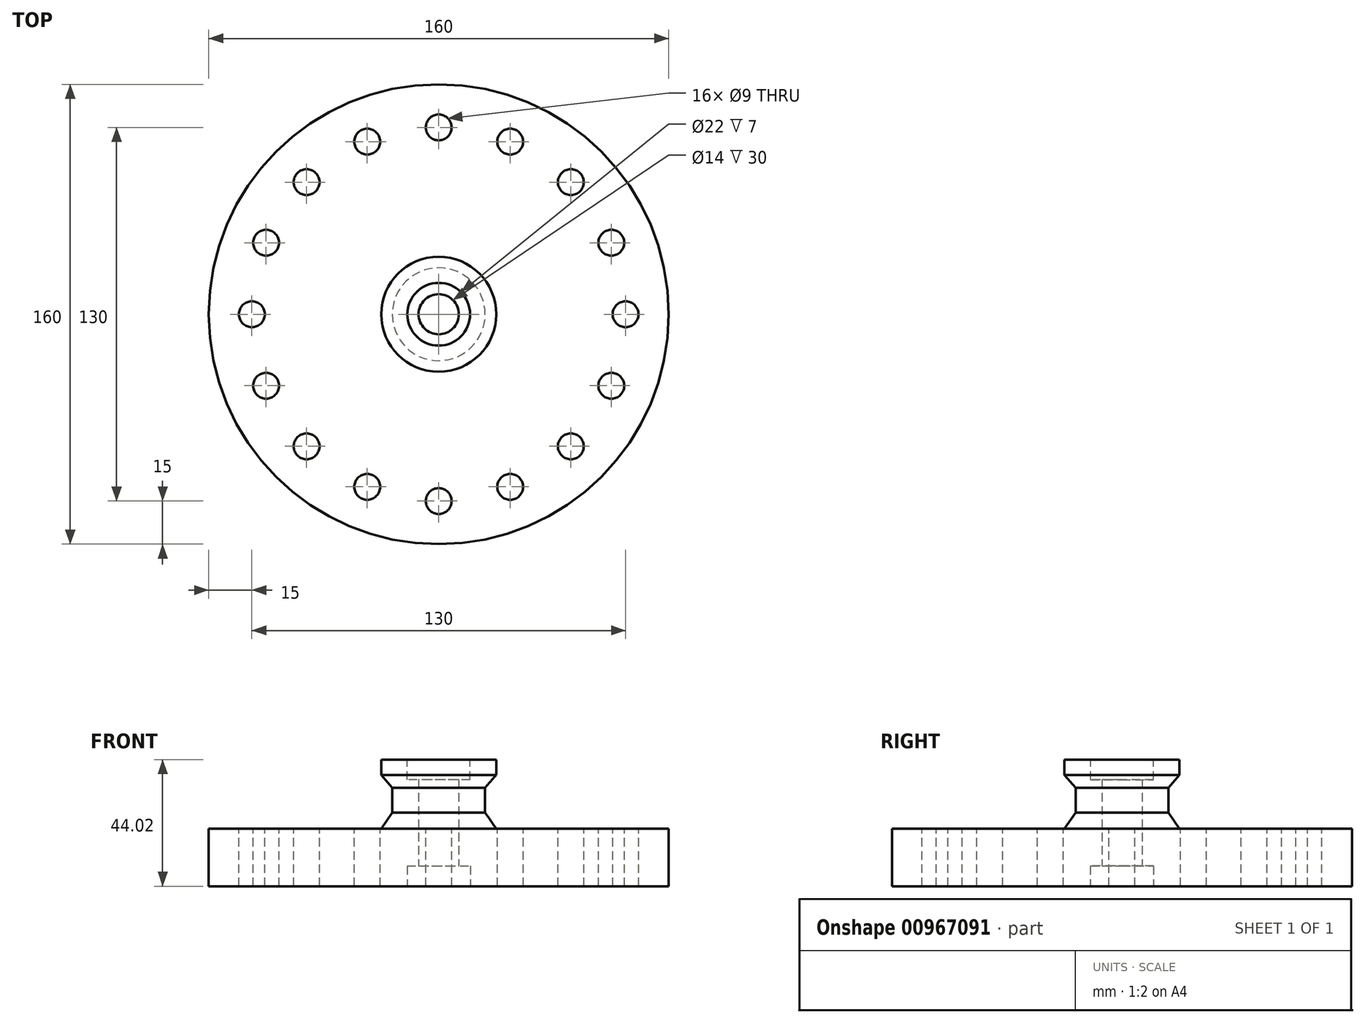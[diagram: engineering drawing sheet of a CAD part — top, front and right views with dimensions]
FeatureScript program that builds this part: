
annotation { "Feature Type Name" : "Feature", "Feature Type Description" : "" }
export const myFeature = defineFeature(function(context is Context, id is Id, definition is map)
    precondition{}
    {
        {
            var Q0;
            Q0=qCreatedBy(makeId("Front.planeOp"),FACE);
            var sketch = newSketch(context, id + "F0", { "sketchPlane" : qUnion([Q0])});
            skLineSegment(sketch, "E0.bottom", {"start": v(-80, 20) * mm, "end": v(-20, 20) * mm});
            skLineSegment(sketch, "E0.top", {"start": v(-80, 0) * mm, "end": v(0, 0) * mm});
            skLineSegment(sketch, "E0.left", {"start": v(-80, 20) * mm, "end": v(-80, 0) * mm});
            skLineSegment(sketch, "E0.right", {"start": v(0, 20) * mm, "end": v(0, 0) * mm});
            skLineSegment(sketch, "E1.left", {"start": v(-20, 38.7) * mm, "end": v(-20, 44.02) * mm});
            skLineSegment(sketch, "E1.right", {"start": v(0, 20) * mm, "end": v(0, 37) * mm});
            skLineSegment(sketch, "E2", {"start": v(0, 100.53) * mm, "end": v(0, 55) * mm, "construction": true});
            skLineSegment(sketch, "E3", {"start": v(-20, 38.7) * mm, "end": v(-16.15, 34.3) * mm});
            skLineSegment(sketch, "E4", {"start": v(-16.15, 34.3) * mm, "end": v(-16.15, 25.61) * mm});
            skLineSegment(sketch, "E5", {"start": v(-16.15, 25.61) * mm, "end": v(-20, 20) * mm});
            skLineSegment(sketch, "E6.bottom", {"start": v(0, 0) * mm, "end": v(-11, 0) * mm});
            skLineSegment(sketch, "E6.top", {"start": v(0, 7) * mm, "end": v(-11, 7) * mm});
            skLineSegment(sketch, "E6.left", {"start": v(0, 0) * mm, "end": v(0, 7) * mm});
            skLineSegment(sketch, "E6.right", {"start": v(-11, 0) * mm, "end": v(-11, 7) * mm});
            skLineSegment(sketch, "E7.top", {"start": v(0, 37) * mm, "end": v(-10.9, 37) * mm});
            skLineSegment(sketch, "E7.right", {"start": v(-10.9, 44) * mm, "end": v(-10.9, 37) * mm});
            skLineSegment(sketch, "E8", {"start": v(-10.9, 44) * mm, "end": v(-20, 44.02) * mm});
            skLineSegment(sketch, "E9.trimOffspring", {"start": v(0, 37) * mm, "end": v(0, -29.96) * mm, "construction": true});
            skSolve(sketch);
        }
        {
            var Q0;
            Q0 = qSketchRegion(id + "F0", true);
            var Q1;
            Q1=sQuery(id+"F0.wireOp",EDGE,"E2");
            revolve(context, id + "F1", {"surfaceOperationType" : NewSurfaceOperationType.NEW, "entities" : qUnion([Q0]), "axis" : qUnion([Q1]), "revolveType" : RevolveType.FULL});
        }
        {
            var Q0;
            Q0=makeQuery(id+"F1.opRevolve","SWEPT_FACE",FACE,{"disambiguationData":[OSD([sQuery(id+"F0.wireOp",EDGE,"E0.top")])]});
            var sketch = newSketch(context, id + "F2", { "sketchPlane" : qUnion([Q0])});
            skCircle(sketch, "E10", {"center": v(0, 0) * mm, "radius": 11 * mm});
            skSolve(sketch);
        }
        {
            var Q0;
            Q0 = qSketchRegion(id + "F2", true);
            extrude(context, id + "F3", {"entities" : qUnion([Q0]), "operationType" : NewBodyOperationType.REMOVE, "oppositeDirection" : true, "depth" : 7 * mm, "offsetDistance" : 25 * mm});
        }
        {
            var Q0;
            Q0=makeQuery(id+"F3.boolean.opBoolean","COPY",FACE,{"derivedFrom":makeQuery(id+"F3.opExtrude","CAP_FACE",FACE,{"disambiguationData":[OSD([sQuery(id+"F2.wireOp",EDGE,"E10")])],"isStart":false})});
            var sketch = newSketch(context, id + "F4", { "sketchPlane" : qUnion([Q0])});
            skCircle(sketch, "E11", {"center": v(0, 0) * mm, "radius": 7 * mm});
            skSolve(sketch);
        }
        {
            var Q0;
            Q0 = qSketchRegion(id + "F4", true);
            extrude(context, id + "F5", {"entities" : qUnion([Q0]), "operationType" : NewBodyOperationType.REMOVE, "oppositeDirection" : true, "depth" : 80 * mm, "offsetDistance" : 25 * mm});
        }
        {
            var Q0;
            Q0=makeQuery(id+"F1.opRevolve","SWEPT_FACE",FACE,{"disambiguationData":[OSD([sQuery(id+"F0.wireOp",EDGE,"E0.bottom")])]});
            var sketch = newSketch(context, id + "F6", { "sketchPlane" : qUnion([Q0])});
            skCircle(sketch, "E12", {"center": v(0, 65) * mm, "radius": 4.5 * mm});
            skCircle(sketch, "E13.1.0", {"center": v(-24.87, 60.05) * mm, "radius": 4.5 * mm});
            skCircle(sketch, "E13.2.0", {"center": v(-45.96, 45.96) * mm, "radius": 4.5 * mm});
            skCircle(sketch, "E13.3.0", {"center": v(-60.05, 24.87) * mm, "radius": 4.5 * mm});
            skCircle(sketch, "E13.4.0", {"center": v(-65, 0) * mm, "radius": 4.5 * mm});
            skCircle(sketch, "E13.5.0", {"center": v(-60.05, -24.87) * mm, "radius": 4.5 * mm});
            skCircle(sketch, "E13.6.0", {"center": v(-45.96, -45.96) * mm, "radius": 4.5 * mm});
            skCircle(sketch, "E13.7.0", {"center": v(-24.87, -60.05) * mm, "radius": 4.5 * mm});
            skCircle(sketch, "E13.8.0", {"center": v(0, -65) * mm, "radius": 4.5 * mm});
            skCircle(sketch, "E13.9.0", {"center": v(24.87, -60.05) * mm, "radius": 4.5 * mm});
            skCircle(sketch, "E13.10.0", {"center": v(45.96, -45.96) * mm, "radius": 4.5 * mm});
            skCircle(sketch, "E13.11.0", {"center": v(60.05, -24.87) * mm, "radius": 4.5 * mm});
            skCircle(sketch, "E13.12.0", {"center": v(65, 0) * mm, "radius": 4.5 * mm});
            skCircle(sketch, "E13.13.0", {"center": v(60.05, 24.87) * mm, "radius": 4.5 * mm});
            skCircle(sketch, "E13.14.0", {"center": v(45.96, 45.96) * mm, "radius": 4.5 * mm});
            skCircle(sketch, "E13.15.0", {"center": v(24.87, 60.05) * mm, "radius": 4.5 * mm});
            skPoint(sketch, "E13.center", {"position": v(0, 0) * mm});
            skSolve(sketch);
        }
        {
            var Q0;
            Q0=makeQuery(id+"F6.imprint","IMPRINT",FACE,{"disambiguationData":[TD([[makeQuery(id+"F6.imprint","IMPRINT",EDGE,{"derivedFrom":sQuery(id+"F6.wireOp",EDGE,"E13.2.0")}),1.0]])]});
            var Q1;
            Q1=makeQuery(id+"F6.imprint","IMPRINT",FACE,{"disambiguationData":[TD([[makeQuery(id+"F6.imprint","IMPRINT",EDGE,{"derivedFrom":sQuery(id+"F6.wireOp",EDGE,"E13.1.0")}),1.0]])]});
            var Q2;
            Q2=makeQuery(id+"F6.imprint","IMPRINT",FACE,{"disambiguationData":[TD([[makeQuery(id+"F6.imprint","IMPRINT",EDGE,{"derivedFrom":sQuery(id+"F6.wireOp",EDGE,"E12")}),1.0]])]});
            var Q3;
            Q3=makeQuery(id+"F6.imprint","IMPRINT",FACE,{"disambiguationData":[TD([[makeQuery(id+"F6.imprint","IMPRINT",EDGE,{"derivedFrom":sQuery(id+"F6.wireOp",EDGE,"E13.15.0")}),1.0]])]});
            var Q4;
            Q4=makeQuery(id+"F6.imprint","IMPRINT",FACE,{"disambiguationData":[TD([[makeQuery(id+"F6.imprint","IMPRINT",EDGE,{"derivedFrom":sQuery(id+"F6.wireOp",EDGE,"E13.14.0")}),1.0]])]});
            var Q5;
            Q5=makeQuery(id+"F6.imprint","IMPRINT",FACE,{"disambiguationData":[TD([[makeQuery(id+"F6.imprint","IMPRINT",EDGE,{"derivedFrom":sQuery(id+"F6.wireOp",EDGE,"E13.13.0")}),1.0]])]});
            var Q6;
            Q6=makeQuery(id+"F6.imprint","IMPRINT",FACE,{"disambiguationData":[TD([[makeQuery(id+"F6.imprint","IMPRINT",EDGE,{"derivedFrom":sQuery(id+"F6.wireOp",EDGE,"E13.12.0")}),1.0]])]});
            var Q7;
            Q7=makeQuery(id+"F6.imprint","IMPRINT",FACE,{"disambiguationData":[TD([[makeQuery(id+"F6.imprint","IMPRINT",EDGE,{"derivedFrom":sQuery(id+"F6.wireOp",EDGE,"E13.11.0")}),1.0]])]});
            var Q8;
            Q8=makeQuery(id+"F6.imprint","IMPRINT",FACE,{"disambiguationData":[TD([[makeQuery(id+"F6.imprint","IMPRINT",EDGE,{"derivedFrom":sQuery(id+"F6.wireOp",EDGE,"E13.10.0")}),1.0]])]});
            var Q9;
            Q9=makeQuery(id+"F6.imprint","IMPRINT",FACE,{"disambiguationData":[TD([[makeQuery(id+"F6.imprint","IMPRINT",EDGE,{"derivedFrom":sQuery(id+"F6.wireOp",EDGE,"E13.9.0")}),1.0]])]});
            var Q10;
            Q10=makeQuery(id+"F6.imprint","IMPRINT",FACE,{"disambiguationData":[TD([[makeQuery(id+"F6.imprint","IMPRINT",EDGE,{"derivedFrom":sQuery(id+"F6.wireOp",EDGE,"E13.8.0")}),1.0]])]});
            var Q11;
            Q11=makeQuery(id+"F6.imprint","IMPRINT",FACE,{"disambiguationData":[TD([[makeQuery(id+"F6.imprint","IMPRINT",EDGE,{"derivedFrom":sQuery(id+"F6.wireOp",EDGE,"E13.7.0")}),1.0]])]});
            var Q12;
            Q12=makeQuery(id+"F6.imprint","IMPRINT",FACE,{"disambiguationData":[TD([[makeQuery(id+"F6.imprint","IMPRINT",EDGE,{"derivedFrom":sQuery(id+"F6.wireOp",EDGE,"E13.6.0")}),1.0]])]});
            var Q13;
            Q13=makeQuery(id+"F6.imprint","IMPRINT",FACE,{"disambiguationData":[TD([[makeQuery(id+"F6.imprint","IMPRINT",EDGE,{"derivedFrom":sQuery(id+"F6.wireOp",EDGE,"E13.5.0")}),1.0]])]});
            var Q14;
            Q14=makeQuery(id+"F6.imprint","IMPRINT",FACE,{"disambiguationData":[TD([[makeQuery(id+"F6.imprint","IMPRINT",EDGE,{"derivedFrom":sQuery(id+"F6.wireOp",EDGE,"E13.4.0")}),1.0]])]});
            var Q15;
            Q15=makeQuery(id+"F6.imprint","IMPRINT",FACE,{"disambiguationData":[TD([[makeQuery(id+"F6.imprint","IMPRINT",EDGE,{"derivedFrom":sQuery(id+"F6.wireOp",EDGE,"E13.3.0")}),1.0]])]});
            extrude(context, id + "F7", {"entities" : qUnion([Q0, Q1, Q2, Q3, Q4, Q5, Q6, Q7, Q8, Q9, Q10, Q11, Q12, Q13, Q14, Q15]), "operationType" : NewBodyOperationType.REMOVE, "oppositeDirection" : true, "depth" : 41.7 * mm, "offsetDistance" : 25 * mm});
        }
    });
